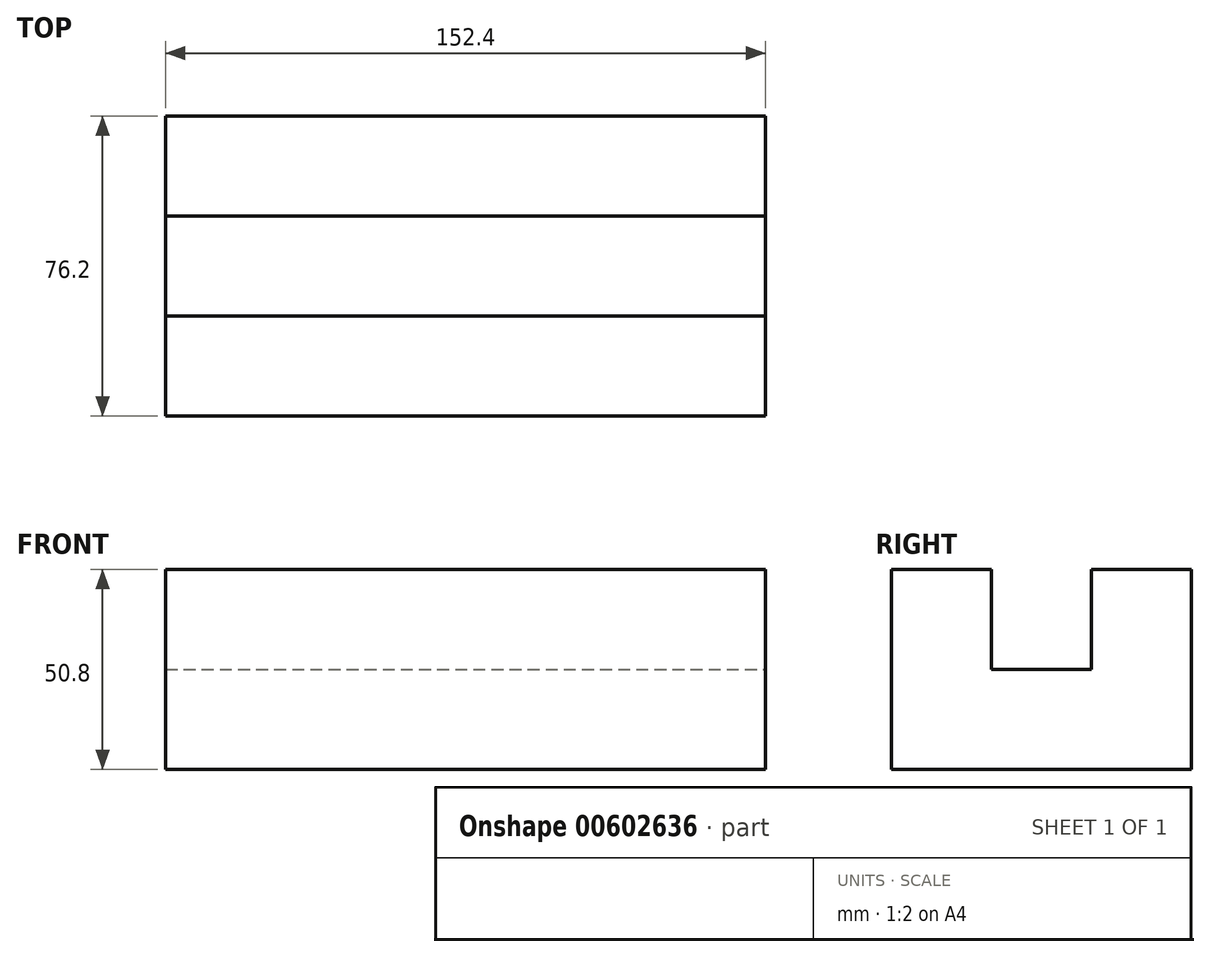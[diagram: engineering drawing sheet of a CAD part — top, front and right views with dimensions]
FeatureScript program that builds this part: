
annotation { "Feature Type Name" : "Feature", "Feature Type Description" : "" }
export const myFeature = defineFeature(function(context is Context, id is Id, definition is map)
    precondition{}
    {
        {
            var Q0;
            Q0=qCreatedBy(makeId("Right.planeOp"),FACE);
            var sketch = newSketch(context, id + "F0", { "sketchPlane" : qUnion([Q0])});
            skLineSegment(sketch, "E0", {"start": v(0, 0) * mm, "end": v(-50.8, 0) * mm});
            skLineSegment(sketch, "E1", {"start": v(-50.8, 0) * mm, "end": v(-50.8, 50.8) * mm});
            skLineSegment(sketch, "E2", {"start": v(-50.8, 50.8) * mm, "end": v(-25.4, 50.8) * mm});
            skLineSegment(sketch, "E3", {"start": v(-25.4, 50.8) * mm, "end": v(-25.4, 25.4) * mm});
            skLineSegment(sketch, "E4", {"start": v(-25.4, 25.4) * mm, "end": v(0, 25.4) * mm});
            skLineSegment(sketch, "E5", {"start": v(0, 25.4) * mm, "end": v(0, 50.8) * mm});
            skLineSegment(sketch, "E6", {"start": v(0, 50.8) * mm, "end": v(25.4, 50.8) * mm});
            skLineSegment(sketch, "E7", {"start": v(25.4, 50.8) * mm, "end": v(25.4, 0) * mm});
            skLineSegment(sketch, "E8", {"start": v(25.4, 0) * mm, "end": v(0, 0) * mm});
            skSolve(sketch);
        }
        {
            var Q0;
            Q0 = qSketchRegion(id + "F0", true);
            extrude(context, id + "F1", {"entities" : qUnion([Q0]), "oppositeDirection" : true, "depth" : 152.4 * mm, "offsetDistance" : 25.4 * mm});
        }
    });
